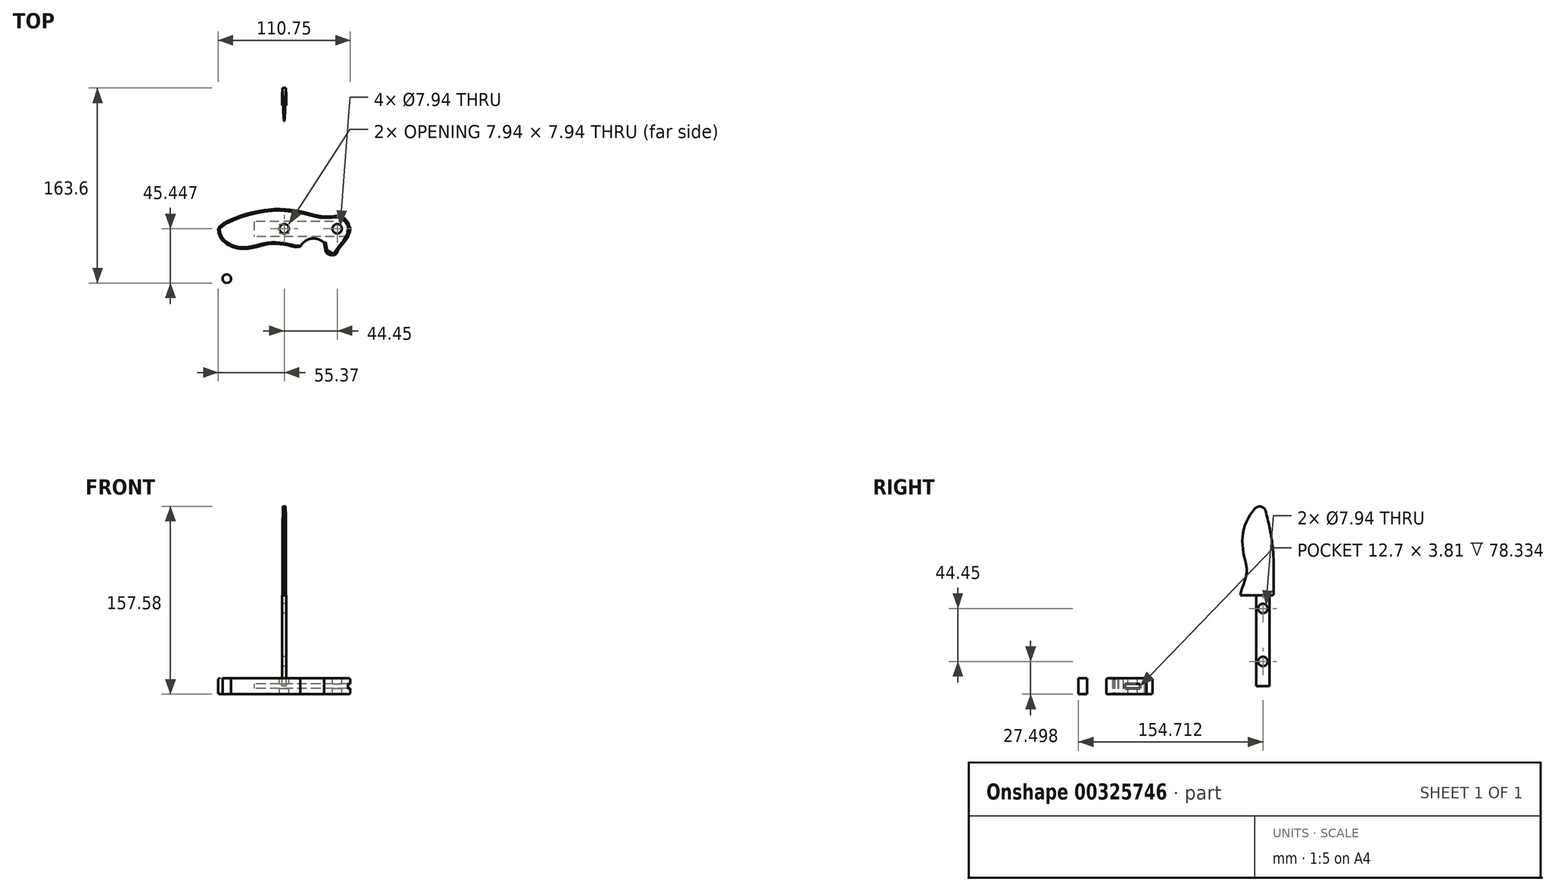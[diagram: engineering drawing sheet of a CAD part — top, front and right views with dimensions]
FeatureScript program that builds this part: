
annotation { "Feature Type Name" : "Feature", "Feature Type Description" : "" }
export const myFeature = defineFeature(function(context is Context, id is Id, definition is map)
    precondition{}
    {
        {
            var Q0;
            Q0=qCreatedBy(makeId("Top.planeOp"),FACE);
            var sketch = newSketch(context, id + "F0", { "sketchPlane" : qUnion([Q0])});
            skLineSegment(sketch, "E0.bottom", {"start": v(-55.37, 19.05) * mm, "end": v(55.37, 19.05) * mm, "construction": true});
            skLineSegment(sketch, "E0.top", {"start": v(-55.37, -19.05) * mm, "end": v(55.37, -19.05) * mm, "construction": true});
            skLineSegment(sketch, "E0.left", {"start": v(-55.37, 19.05) * mm, "end": v(-55.37, -19.05) * mm, "construction": true});
            skLineSegment(sketch, "E0.right", {"start": v(55.37, 19.05) * mm, "end": v(55.37, -19.05) * mm, "construction": true});
            skPoint(sketch, "E0.middle", {"position": v(0, 0) * mm});
            skLineSegment(sketch, "E1", {"start": v(-55.37, 2.67) * mm, "end": v(55.37, 2.67) * mm, "construction": true});
            skFitSpline(sketch, "E2", {"points": [v(-55.37, 2.67) * mm, v(-10.29, 19.05) * mm, v(33.53, 12.95) * mm, v(45.6, 13.97) * mm, v(47.38, 13.97) * mm, v(55.37, 2.67) * mm, v(45.21, -15.24) * mm, v(42.67, -19.05) * mm, v(35.69, -17.78) * mm, v(33.64, -9.2) * mm], "startDerivative": vector(0, 74.85) * mm, "endDerivative": vector(-36.27, 89.98) * mm});
            skArc(sketch, "E3", {"start": v(33.64, -9.2) * mm, "mid": v(22.67, -5.61) * mm, "end": v(13.32, -12.4) * mm});
            skFitSpline(sketch, "E4", {"points": [v(-55.37, 2.67) * mm, v(-36.32, -14.1) * mm, v(-11.91, -10.03) * mm, v(6.86, -12.1) * mm, v(13.32, -12.4) * mm], "startDerivative": vector(0, -104.62) * mm, "endDerivative": vector(34.3, 18.6) * mm});
            skSolve(sketch);
        }
        {
            var Q0;
            Q0=makeQuery(id+"F0.imprint","IMPRINT",FACE,{"disambiguationData":[TD([[makeQuery(id+"F0.imprint","IMPRINT",EDGE,{"derivedFrom":sQuery(id+"F0.wireOp",EDGE,"E2")}),-1.0]])]});
            extrude(context, id + "F1", {"entities" : qUnion([Q0]), "depth" : 6.67 * mm, "hasSecondDirection" : true, "secondDirectionOppositeDirection" : true, "secondDirectionDepth" : 6.67 * mm});
        }
        {
            var Q0;
            Q0=makeQuery(id+"F1.opExtrude","CAP_EDGE",EDGE,{"disambiguationData":[OSD([sQuery(id+"F0.wireOp",EDGE,"E4")])],"isStart":false});
            var Q1;
            Q1=makeQuery(id+"F1.opExtrude","CAP_EDGE",EDGE,{"disambiguationData":[OSD([sQuery(id+"F0.wireOp",EDGE,"E2")])],"isStart":false});
            var Q2;
            Q2=makeQuery(id+"F1.opExtrude","CAP_EDGE",EDGE,{"disambiguationData":[OSD([sQuery(id+"F0.wireOp",EDGE,"E3")])],"isStart":false});
            fillet(context, id + "F2", {"entities" : qUnion([Q0, Q1, Q2]), "radius" : 1.27 * mm, "tangentPropagation" : true, "allowEdgeOverflow" : false});
        }
        {
            var Q0;
            Q0=makeQuery(id+"F1.opExtrude","CAP_EDGE",EDGE,{"disambiguationData":[OSD([sQuery(id+"F0.wireOp",EDGE,"E2")])],"isStart":true});
            var Q1;
            Q1=makeQuery(id+"F1.opExtrude","CAP_EDGE",EDGE,{"disambiguationData":[OSD([sQuery(id+"F0.wireOp",EDGE,"E3")])],"isStart":true});
            var Q2;
            Q2=makeQuery(id+"F1.opExtrude","CAP_EDGE",EDGE,{"disambiguationData":[OSD([sQuery(id+"F0.wireOp",EDGE,"E4")])],"isStart":true});
            fillet(context, id + "F3", {"entities" : qUnion([Q0, Q1, Q2]), "radius" : 1.27 * mm, "tangentPropagation" : true, "allowEdgeOverflow" : false});
        }
        {
            var Q0;
            Q0=qCreatedBy(makeId("Right.planeOp"),FACE);
            var sketch = newSketch(context, id + "F4", { "sketchPlane" : qUnion([Q0])});
            skLineSegment(sketch, "E5.bottom", {"start": v(8.9, 1.9) * mm, "end": v(-3.81, 1.9) * mm});
            skLineSegment(sketch, "E5.top", {"start": v(8.9, -1.9) * mm, "end": v(-3.81, -1.9) * mm});
            skLineSegment(sketch, "E5.left", {"start": v(8.9, 1.9) * mm, "end": v(8.9, -1.9) * mm});
            skLineSegment(sketch, "E5.right", {"start": v(-3.81, 1.9) * mm, "end": v(-3.81, -1.9) * mm});
            skPoint(sketch, "E5.middle", {"position": v(0, 0) * mm});
            skSolve(sketch);
        }
        {
            var Q0;
            Q0=makeQuery(id+"F4.imprint","IMPRINT",FACE,{"disambiguationData":[TD([[makeQuery(id+"F4.imprint","IMPRINT",EDGE,{"derivedFrom":sQuery(id+"F4.wireOp",EDGE,"E5.bottom")}),1.0]])]});
            var Q1;
            Q1=makeQuery(id+"F1.opExtrude","SWEPT_FACE",FACE,{"disambiguationData":[OSD([sQuery(id+"F0.wireOp",EDGE,"E2")])]});
            extrude(context, id + "F5", {"entities" : qUnion([Q0]), "operationType" : NewBodyOperationType.REMOVE, "endBound" : BoundingType.UP_TO_SURFACE, "endBoundEntityFace" : qUnion([Q1]), "depth" : 25.4 * mm, "hasSecondDirection" : true, "secondDirectionOppositeDirection" : true, "secondDirectionDepth" : 25.4 * mm});
        }
        {
            var Q0;
            Q0=makeQuery(id+"F1.opExtrude","CAP_FACE",FACE,{"disambiguationData":[OSD([sQuery(id+"F0.wireOp",EDGE,"E2"),sQuery(id+"F0.wireOp",EDGE,"E3"),sQuery(id+"F0.wireOp",EDGE,"E4")])],"isStart":false});
            var sketch = newSketch(context, id + "F6", { "sketchPlane" : qUnion([Q0])});
            skCircle(sketch, "E6", {"center": v(0, 2.67) * mm, "radius": 3.97 * mm});
            skCircle(sketch, "E7", {"center": v(44.45, 2.67) * mm, "radius": 3.97 * mm});
            skSolve(sketch);
        }
        {
            var Q0;
            Q0=makeQuery(id+"F6.imprint","IMPRINT",FACE,{"disambiguationData":[TD([[makeQuery(id+"F6.imprint","IMPRINT",EDGE,{"derivedFrom":sQuery(id+"F6.wireOp",EDGE,"E6")}),1.0]])]});
            var Q1;
            Q1=makeQuery(id+"F6.imprint","IMPRINT",FACE,{"disambiguationData":[TD([[makeQuery(id+"F6.imprint","IMPRINT",EDGE,{"derivedFrom":sQuery(id+"F6.wireOp",EDGE,"E7")}),1.0]])]});
            extrude(context, id + "F7", {"entities" : qUnion([Q0, Q1]), "operationType" : NewBodyOperationType.REMOVE, "endBound" : BoundingType.THROUGH_ALL, "oppositeDirection" : true, "depth" : 25.4 * mm});
        }
        {
            var Q0;
            Q0=qCreatedBy(makeId("Top.planeOp"),FACE);
            var sketch = newSketch(context, id + "F8", { "sketchPlane" : qUnion([Q0])});
            skCircle(sketch, "E8", {"center": v(-48.18, -39.2) * mm, "radius": 3.58 * mm});
            skSolve(sketch);
        }
        {
            var Q0;
            Q0=makeQuery(id+"F8.imprint","IMPRINT",FACE,{"disambiguationData":[TD([[makeQuery(id+"F8.imprint","IMPRINT",EDGE,{"derivedFrom":sQuery(id+"F8.wireOp",EDGE,"E8")}),1.0]])]});
            var Q1;
            Q1=makeQuery(id+"F1.opExtrude","CAP_FACE",FACE,{"disambiguationData":[OSD([sQuery(id+"F0.wireOp",EDGE,"E2"),sQuery(id+"F0.wireOp",EDGE,"E3"),sQuery(id+"F0.wireOp",EDGE,"E4")])],"isStart":false});
            var Q2;
            Q2=makeQuery(id+"F1.opExtrude","CAP_FACE",FACE,{"disambiguationData":[OSD([sQuery(id+"F0.wireOp",EDGE,"E2"),sQuery(id+"F0.wireOp",EDGE,"E3"),sQuery(id+"F0.wireOp",EDGE,"E4")])],"isStart":true});
            extrude(context, id + "F9", {"entities" : qUnion([Q0]), "endBound" : BoundingType.UP_TO_SURFACE, "endBoundEntityFace" : qUnion([Q1]), "depth" : 25.4 * mm, "hasSecondDirection" : true, "secondDirectionBound" : SecondDirectionBoundingType.UP_TO_SURFACE, "secondDirectionOppositeDirection" : true, "secondDirectionBoundEntityFace" : qUnion([Q2]), "secondDirectionDepth" : 25.4 * mm});
        }
        {
            var Q0;
            Q0=qCreatedBy(makeId("Right.planeOp"),FACE);
            var sketch = newSketch(context, id + "F10", { "sketchPlane" : qUnion([Q0])});
            skLineSegment(sketch, "E9.bottom", {"start": v(106.38, 0) * mm, "end": v(117.49, 0) * mm});
            skLineSegment(sketch, "E9.top", {"start": v(106.38, 76.2) * mm, "end": v(117.49, 76.2) * mm});
            skLineSegment(sketch, "E9.left", {"start": v(106.38, 0) * mm, "end": v(106.38, 76.2) * mm});
            skLineSegment(sketch, "E9.right", {"start": v(117.49, 0) * mm, "end": v(117.49, 76.2) * mm});
            skLineSegment(sketch, "E10", {"start": v(111.93, 76.2) * mm, "end": v(111.93, 0) * mm, "construction": true});
            skCircle(sketch, "E11", {"center": v(111.93, 65.28) * mm, "radius": 3.97 * mm});
            skCircle(sketch, "E12", {"center": v(111.93, 20.83) * mm, "radius": 3.97 * mm});
            skSolve(sketch);
        }
        {
            var Q0;
            Q0=makeQuery(id+"F10.imprint","IMPRINT",FACE,{"disambiguationData":[TD([[makeQuery(id+"F10.imprint","IMPRINT",EDGE,{"derivedFrom":sQuery(id+"F10.wireOp",EDGE,"E9.bottom")}),1.0]])]});
            extrude(context, id + "F11", {"entities" : qUnion([Q0]), "depth" : 1.65 * mm, "hasSecondDirection" : true, "secondDirectionOppositeDirection" : true, "secondDirectionDepth" : 1.65 * mm});
        }
        {
            var Q0;
            Q0=makeQuery(id+"F11.opExtrude","SWEPT_FACE",FACE,{"disambiguationData":[OSD([sQuery(id+"F10.wireOp",EDGE,"E9.top")])]});
            var sketch = newSketch(context, id + "F12", { "sketchPlane" : qUnion([Q0])});
            skLineSegment(sketch, "E13", {"start": v(0, 111.93) * mm, "end": v(0, 92.88) * mm, "construction": true});
            skPoint(sketch, "E13.startSnap0", {"position": v(0, 106.38) * mm});
            skLineSegment(sketch, "E14", {"start": v(1.65, 111.93) * mm, "end": v(-1.65, 111.93) * mm, "construction": true});
            skLineSegment(sketch, "E15", {"start": v(0, 111.93) * mm, "end": v(0, 120.82) * mm, "construction": true});
            skLineSegment(sketch, "E16", {"start": v(0, 120.82) * mm, "end": v(1.46, 120.82) * mm});
            skFitSpline(sketch, "E17", {"points": [v(0, 92.88) * mm, v(0.37, 95.2) * mm, v(1.46, 120.82) * mm], "startDerivative": vector(1.63, 7.27) * mm, "endDerivative": vector(1.34, 42.35) * mm});
            skFitSpline(sketch, "E18.MirrorCS", {"points": [v(0, 92.88) * mm, v(-0.37, 95.2) * mm, v(-1.46, 120.82) * mm], "startDerivative": vector(-1.63, 7.27) * mm, "endDerivative": vector(-1.34, 42.35) * mm});
            skLineSegment(sketch, "E19.MirrorCS", {"start": v(0, 120.82) * mm, "end": v(-1.46, 120.82) * mm});
            skSolve(sketch);
        }
        {
            var Q0;
            {var subQ0=sQuery(id+"F12.wireOp",EDGE,"E18.MirrorCS");var subQ1=sQuery(id+"F12.wireOp",EDGE,"E17");var subQ2=makeQuery(id+"F12.imprint","INTERSECT",VERTEX,{"derivedFrom":[subQ1,subQ0]});Q0=makeQuery(id+"F12.imprint","IMPRINT",FACE,{"disambiguationData":[TD([[makeQuery(id+"F12.imprint","IMPRINT",EDGE,{"disambiguationData":[TD([[subQ2,-1.0]])],"derivedFrom":subQ1}),1.0]])]});}
            var Q1;
            {var subQ0=sQuery(id+"F12.wireOp",EDGE,"E17");var subQ1=sQuery(id+"F10.wireOp",EDGE,"E9.top");var subQ2=makeQuery(id+"F11.opExtrude","SWEPT_EDGE",EDGE,{"disambiguationData":[OSD([subQ1,sQuery(id+"F10.wireOp",EDGE,"E9.left")])]});var subQ3=makeQuery(id+"F12.imprint","INTERSECT",VERTEX,{"derivedFrom":[subQ2,subQ0]});Q1=makeQuery(id+"F12.imprint","IMPRINT",FACE,{"disambiguationData":[TD([[makeQuery(id+"F12.imprint","IMPRINT",EDGE,{"disambiguationData":[TD([[subQ3,-1.0]])],"derivedFrom":subQ0}),1.0]])]});}
            var Q2;
            {var subQ5=sQuery(id+"F12.wireOp",EDGE,"E16");Q2=makeQuery(id+"F12.imprint","IMPRINT",FACE,{"disambiguationData":[TD([[makeQuery(id+"F12.imprint","IMPRINT",EDGE,{"derivedFrom":subQ5}),-1.0]])]});}
            extrude(context, id + "F13", {"entities" : qUnion([Q0, Q1, Q2]), "operationType" : NewBodyOperationType.ADD, "depth" : 78.74 * mm});
        }
        {
            var Q0;
            Q0=qCreatedBy(makeId("Right.planeOp"),FACE);
            var sketch = newSketch(context, id + "F14", { "sketchPlane" : qUnion([Q0])});
            skLineSegment(sketch, "E20", {"start": v(111.93, 65.28) * mm, "end": v(111.93, 154.94) * mm, "construction": true});
            skFitSpline(sketch, "E21", {"points": [v(111.93, 154.94) * mm, v(96.35, 133.2) * mm, v(96.2, 109.28) * mm, v(98.44, 95.45) * mm, v(92.88, 76.2) * mm], "startDerivative": vector(-68.33, -45.32) * mm, "endDerivative": vector(-17.62, -86.98) * mm});
            skFitSpline(sketch, "E22", {"points": [v(111.93, 154.94) * mm, v(120.82, 107.44) * mm, v(119.18, 86.03) * mm, v(120.82, 76.2) * mm], "startDerivative": vector(32.2, -106.48) * mm, "endDerivative": vector(25, -37.51) * mm});
            skLineSegment(sketch, "E23", {"start": v(92.88, 76.2) * mm, "end": v(92.88, 159.3) * mm});
            skLineSegment(sketch, "E24", {"start": v(92.88, 159.3) * mm, "end": v(120.82, 159.3) * mm});
            skLineSegment(sketch, "E25", {"start": v(120.82, 159.3) * mm, "end": v(120.82, 76.2) * mm});
            skSolve(sketch);
        }
        {
            var Q0;
            {var subQ1=sQuery(id+"F14.wireOp",EDGE,"E21");Q0=makeQuery(id+"F14.imprint","IMPRINT",FACE,{"disambiguationData":[TD([[makeQuery(id+"F14.imprint","IMPRINT",EDGE,{"derivedFrom":subQ1}),-1.0]])]});}
            var Q1;
            {var subQ0=sQuery(id+"F14.wireOp",EDGE,"E25");var subQ1=sQuery(id+"F14.wireOp",EDGE,"E22");var subQ2=makeQuery(id+"F14.imprint","INTERSECT",VERTEX,{"disambiguationData":[OD(0.0)],"derivedFrom":[subQ1,subQ0]});Q1=makeQuery(id+"F14.imprint","IMPRINT",FACE,{"disambiguationData":[TD([[makeQuery(id+"F14.imprint","IMPRINT",EDGE,{"disambiguationData":[TD([[subQ2,1.0]])],"derivedFrom":subQ1}),1.0]])]});}
            extrude(context, id + "F15", {"entities" : qUnion([Q0, Q1]), "operationType" : NewBodyOperationType.REMOVE, "endBound" : BoundingType.THROUGH_ALL, "oppositeDirection" : true, "depth" : 25.4 * mm, "hasSecondDirection" : true, "secondDirectionBound" : SecondDirectionBoundingType.THROUGH_ALL, "secondDirectionOppositeDirection" : false, "secondDirectionDepth" : 25.4 * mm});
        }
        {
            var Q0;
            {var subQ0=sQuery(id+"F14.wireOp",EDGE,"E25");var subQ1=sQuery(id+"F14.wireOp",EDGE,"E22");Q0=makeQuery(id+"F15.boolean.opBoolean","MERGE",EDGE,{"derivedFrom":[makeQuery(id+"F13.opExtrude","CAP_EDGE",EDGE,{"disambiguationData":[OSD([sQuery(id+"F12.wireOp",EDGE,"E16"),sQuery(id+"F12.wireOp",EDGE,"E19.MirrorCS")])],"isStart":true}),makeQuery(id+"F15.opExtrude","SWEPT_EDGE",EDGE,{"disambiguationData":[OSD([subQ1,subQ0]),TDD([makeQuery(id+"F14.imprint","INTERSECT",VERTEX,{"disambiguationData":[OD(0.0)],"derivedFrom":[subQ1,subQ0]})])]})]});}
            fillet(context, id + "F16", {"entities" : qUnion([Q0]), "radius" : 1.27 * mm, "tangentPropagation" : true, "allowEdgeOverflow" : false});
        }
        {
            var Q0;
            Q0=makeQuery(id+"F15.boolean.opBoolean","COPY",EDGE,{"derivedFrom":makeQuery(id+"F15.opExtrude","SWEPT_EDGE",EDGE,{"disambiguationData":[OSD([sQuery(id+"F14.wireOp",EDGE,"E21"),sQuery(id+"F14.wireOp",EDGE,"E22")])]})});
            fillet(context, id + "F17", {"entities" : qUnion([Q0]), "radius" : 5.08 * mm, "tangentPropagation" : true, "allowEdgeOverflow" : false});
        }
    });
